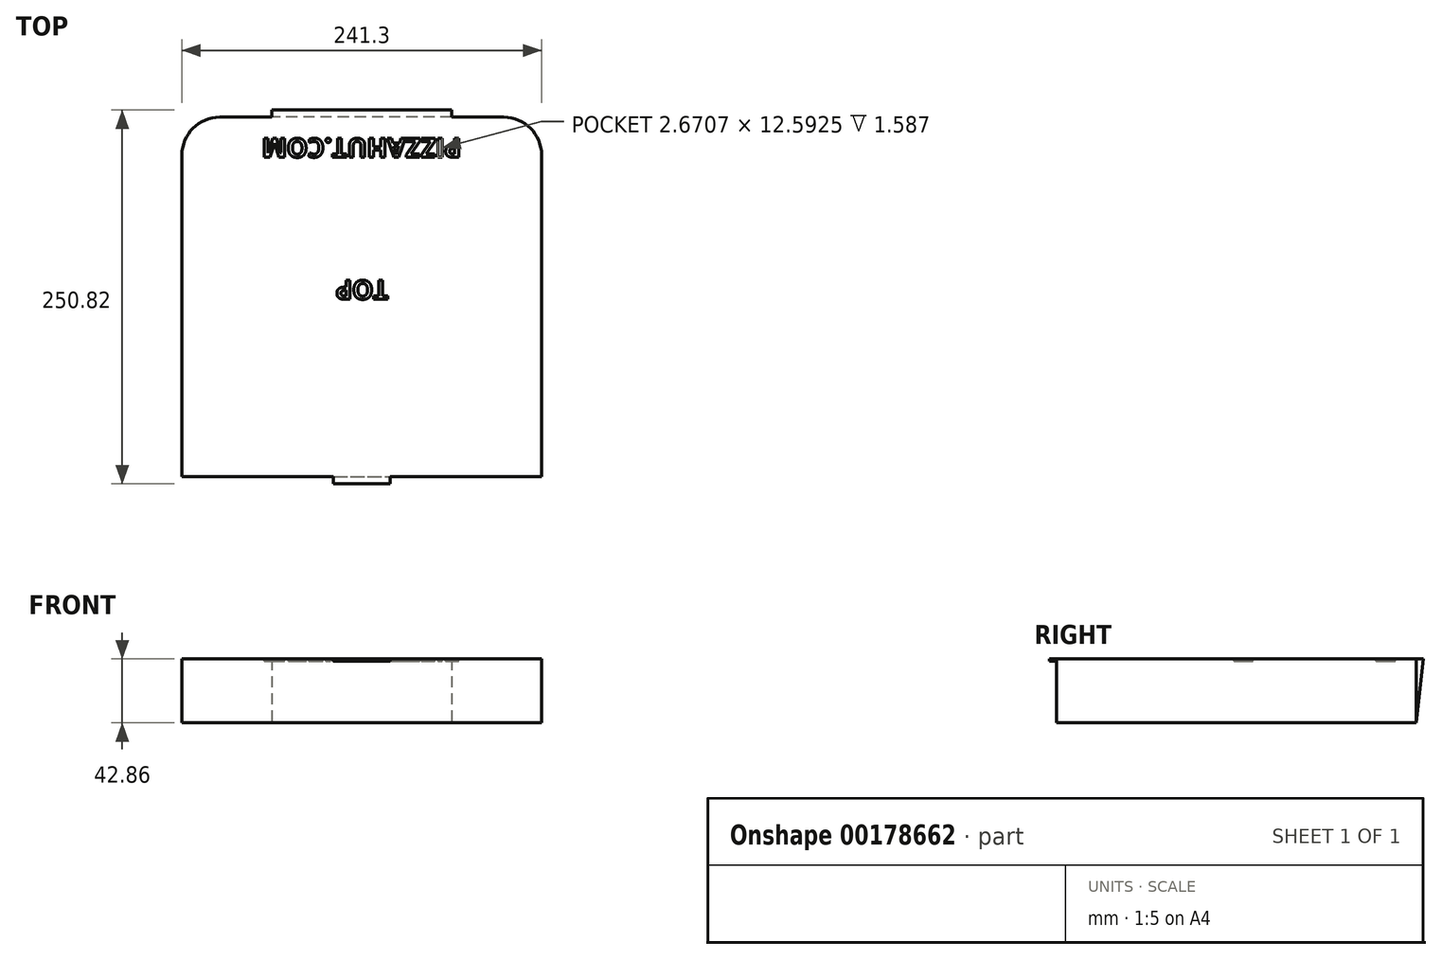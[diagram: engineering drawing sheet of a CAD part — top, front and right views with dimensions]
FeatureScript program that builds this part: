
annotation { "Feature Type Name" : "Feature", "Feature Type Description" : "" }
export const myFeature = defineFeature(function(context is Context, id is Id, definition is map)
    precondition{}
    {
        {
            var Q0;
            Q0=qCreatedBy(makeId("Top.planeOp"),FACE);
            var sketch = newSketch(context, id + "F0", { "sketchPlane" : qUnion([Q0])});
            skLineSegment(sketch, "E0.bottom", {"start": v(0, 0) * mm, "end": v(101.6, 0) * mm});
            skLineSegment(sketch, "E0.top", {"start": v(25.4, 241.3) * mm, "end": v(60.32, 241.3) * mm});
            skLineSegment(sketch, "E0.left", {"start": v(0, 0) * mm, "end": v(0, 215.9) * mm});
            skLineSegment(sketch, "E0.right", {"start": v(241.3, 0) * mm, "end": v(241.3, 215.9) * mm});
            skPoint(sketch, "E1", {"position": v(120.65, 0) * mm});
            skLineSegment(sketch, "E2.top", {"start": v(101.6, -4.76) * mm, "end": v(139.7, -4.76) * mm});
            skLineSegment(sketch, "E2.left", {"start": v(101.6, 0) * mm, "end": v(101.6, -4.76) * mm});
            skLineSegment(sketch, "E2.right", {"start": v(139.7, 0) * mm, "end": v(139.7, -4.76) * mm});
            skPoint(sketch, "E3.visualSharp", {"position": v(0, 241.3) * mm});
            skArc(sketch, "E3.filletArc", {"start": v(25.4, 241.3) * mm, "mid": v(7.44, 233.86) * mm, "end": v(0, 215.9) * mm});
            skPoint(sketch, "E4.visualSharp", {"position": v(241.3, 241.3) * mm});
            skArc(sketch, "E4.filletArc", {"start": v(241.3, 215.9) * mm, "mid": v(233.86, 233.86) * mm, "end": v(215.9, 241.3) * mm});
            skLineSegment(sketch, "E5.bottom", {"start": v(60.32, 246.06) * mm, "end": v(180.97, 246.06) * mm});
            skLineSegment(sketch, "E5.left", {"start": v(60.32, 246.06) * mm, "end": v(60.32, 241.3) * mm});
            skLineSegment(sketch, "E5.right", {"start": v(180.97, 246.06) * mm, "end": v(180.97, 241.3) * mm});
            skPoint(sketch, "E6", {"position": v(120.65, 241.3) * mm});
            skLineSegment(sketch, "E7", {"start": v(180.97, 241.3) * mm, "end": v(215.9, 241.3) * mm});
            skLineSegment(sketch, "E8.trimOffspring", {"start": v(139.7, 0) * mm, "end": v(241.3, 0) * mm});
            skSolve(sketch);
        }
        {
            var Q0;
            Q0 = qSketchRegion(id + "F0", true);
            extrude(context, id + "F1", {"entities" : qUnion([Q0]), "depth" : 42.86 * mm});
        }
        {
            var Q0;
            Q0=makeQuery(id+"F1.opExtrude","SWEPT_FACE",FACE,{"disambiguationData":[OSD([sQuery(id+"F0.wireOp",EDGE,"E5.left")])]});
            var sketch = newSketch(context, id + "F2", { "sketchPlane" : qUnion([Q0])});
            skLineSegment(sketch, "E9", {"start": v(-246.06, 42.86) * mm, "end": v(-241.3, 0) * mm});
            skLineSegment(sketch, "E10", {"start": v(-241.3, 0) * mm, "end": v(-246.06, 0) * mm});
            skLineSegment(sketch, "E11", {"start": v(-246.06, 0) * mm, "end": v(-246.06, 42.86) * mm});
            skSolve(sketch);
        }
        {
            var Q0;
            Q0 = qSketchRegion(id + "F2", true);
            extrude(context, id + "F3", {"entities" : qUnion([Q0]), "operationType" : NewBodyOperationType.REMOVE, "endBound" : BoundingType.THROUGH_ALL, "oppositeDirection" : true, "depth" : 25.4 * mm});
        }
        {
            var Q0;
            Q0=makeQuery(id+"F1.opExtrude","CAP_FACE",FACE,{"disambiguationData":[OSD([sQuery(id+"F0.wireOp",EDGE,"E0.bottom"),sQuery(id+"F0.wireOp",EDGE,"E0.top"),sQuery(id+"F0.wireOp",EDGE,"E0.left"),sQuery(id+"F0.wireOp",EDGE,"E0.right"),sQuery(id+"F0.wireOp",EDGE,"E2.top"),sQuery(id+"F0.wireOp",EDGE,"E2.left"),sQuery(id+"F0.wireOp",EDGE,"E2.right"),sQuery(id+"F0.wireOp",EDGE,"E3.filletArc"),sQuery(id+"F0.wireOp",EDGE,"E4.filletArc"),sQuery(id+"F0.wireOp",EDGE,"E5.bottom"),sQuery(id+"F0.wireOp",EDGE,"E5.left"),sQuery(id+"F0.wireOp",EDGE,"E5.right"),sQuery(id+"F0.wireOp",EDGE,"E7"),sQuery(id+"F0.wireOp",EDGE,"E8.trimOffspring")])],"isStart":true});
            var sketch = newSketch(context, id + "F4", { "sketchPlane" : qUnion([Q0])});
            skLineSegment(sketch, "E12.bottom", {"start": v(101.6, 4.76) * mm, "end": v(139.7, 4.76) * mm});
            skLineSegment(sketch, "E12.top", {"start": v(101.6, 0) * mm, "end": v(139.7, 0) * mm});
            skLineSegment(sketch, "E12.left", {"start": v(101.6, 4.76) * mm, "end": v(101.6, 0) * mm});
            skLineSegment(sketch, "E12.right", {"start": v(139.7, 4.76) * mm, "end": v(139.7, 0) * mm});
            skSolve(sketch);
        }
        {
            var Q0;
            Q0 = qSketchRegion(id + "F4", true);
            extrude(context, id + "F5", {"entities" : qUnion([Q0]), "operationType" : NewBodyOperationType.REMOVE, "oppositeDirection" : true, "depth" : 41.27 * mm});
        }
        {
            var Q0;
            Q0=makeQuery(id+"F1.opExtrude","CAP_FACE",FACE,{"disambiguationData":[OSD([sQuery(id+"F0.wireOp",EDGE,"E0.bottom"),sQuery(id+"F0.wireOp",EDGE,"E0.top"),sQuery(id+"F0.wireOp",EDGE,"E0.left"),sQuery(id+"F0.wireOp",EDGE,"E0.right"),sQuery(id+"F0.wireOp",EDGE,"E2.top"),sQuery(id+"F0.wireOp",EDGE,"E2.left"),sQuery(id+"F0.wireOp",EDGE,"E2.right"),sQuery(id+"F0.wireOp",EDGE,"E3.filletArc"),sQuery(id+"F0.wireOp",EDGE,"E4.filletArc"),sQuery(id+"F0.wireOp",EDGE,"E5.bottom"),sQuery(id+"F0.wireOp",EDGE,"E5.left"),sQuery(id+"F0.wireOp",EDGE,"E5.right"),sQuery(id+"F0.wireOp",EDGE,"E7"),sQuery(id+"F0.wireOp",EDGE,"E8.trimOffspring")])],"isStart":false});
            var sketch = newSketch(context, id + "F6", { "sketchPlane" : qUnion([Q0])});
            skText(sketch, "E13", { "text": "PIZZAHUT.COM", "fontName": "OpenSans-Bold.ttf"});
            skPoint(sketch, "E14", {"position": v(120.65, 227.01) * mm});
            skPoint(sketch, "E14.positionSnap0", {"position": v(120.65, 246.06) * mm});
            skText(sketch, "E15", { "text": "TOP", "fontName": "OpenSans-Bold.ttf"});
            skPoint(sketch, "E16", {"position": v(120.65, 131.76) * mm});
            skPoint(sketch, "E16.positionSnap0", {"position": v(120.65, 223.96) * mm});
            const initialGuessF6  = {"E13": [0.18718, 0.22701, -1, 0, 0.0127], "E15": [0.1385, 0.13176, -1, 0, 0.0127]};
            skSetInitialGuess(sketch, initialGuessF6);
            skSolve(sketch);
        }
        {
            var Q0;
            Q0 = qSketchRegion(id + "F6", true);
            extrude(context, id + "F7", {"entities" : qUnion([Q0]), "operationType" : NewBodyOperationType.REMOVE, "oppositeDirection" : true, "depth" : 1.59 * mm});
        }
    });
